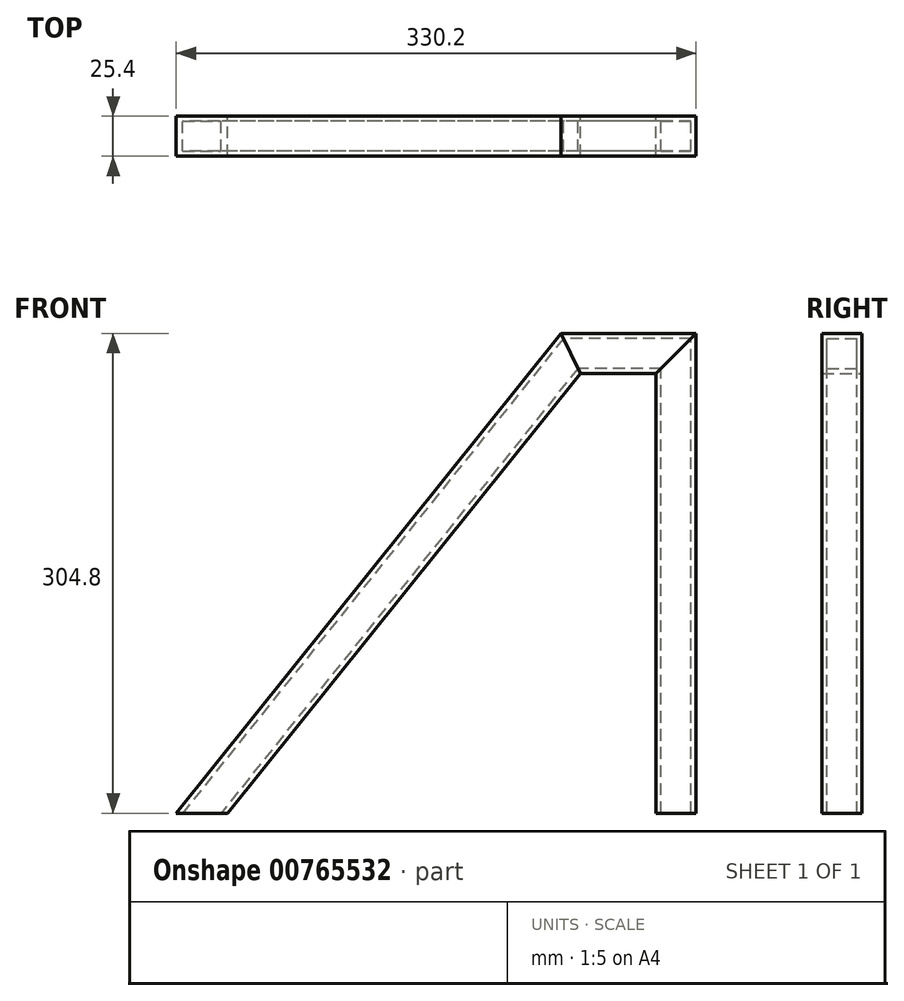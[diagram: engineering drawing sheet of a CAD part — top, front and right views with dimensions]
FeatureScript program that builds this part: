
annotation { "Feature Type Name" : "Feature", "Feature Type Description" : "" }
export const myFeature = defineFeature(function(context is Context, id is Id, definition is map)
    precondition{}
    {
        {
            var Q0;
            Q0=qCreatedBy(makeId("Front.planeOp"),FACE);
            var sketch = newSketch(context, id + "F0", { "sketchPlane" : qUnion([Q0])});
            skLineSegment(sketch, "E0", {"start": v(0, 0) * mm, "end": v(0, 304.8) * mm});
            skLineSegment(sketch, "E1", {"start": v(0, 304.8) * mm, "end": v(-85.72, 304.8) * mm});
            skLineSegment(sketch, "E2", {"start": v(-85.72, 304.8) * mm, "end": v(-330.2, 0) * mm});
            skLineSegment(sketch, "E3.0", {"start": v(-73.54, 279.4) * mm, "end": v(-297.64, 0) * mm});
            skLineSegment(sketch, "E3.1", {"start": v(-25.4, 279.4) * mm, "end": v(-73.54, 279.4) * mm});
            skLineSegment(sketch, "E3.2", {"start": v(-25.4, 0) * mm, "end": v(-25.4, 279.4) * mm});
            skLineSegment(sketch, "E4", {"start": v(-330.2, 0) * mm, "end": v(-297.64, 0) * mm});
            skLineSegment(sketch, "E5", {"start": v(-25.4, 0) * mm, "end": v(0, 0) * mm});
            skLineSegment(sketch, "E6", {"start": v(-25.4, 279.4) * mm, "end": v(0, 304.8) * mm});
            skLineSegment(sketch, "E7", {"start": v(-73.54, 279.4) * mm, "end": v(-85.73, 304.8) * mm});
            skSolve(sketch);
        }
        {
            var Q0;
            Q0=makeQuery(id+"F0.imprint","IMPRINT",FACE,{"disambiguationData":[TD([[makeQuery(id+"F0.imprint","IMPRINT",EDGE,{"derivedFrom":sQuery(id+"F0.wireOp",EDGE,"E2")}),1.0]])]});
            extrude(context, id + "F1", {"entities" : qUnion([Q0]), "depth" : 25.4 * mm, "offsetDistance" : 25.4 * mm, "symmetric" : true});
        }
        {
            var Q0;
            Q0=makeQuery(id+"F0.imprint","IMPRINT",FACE,{"disambiguationData":[TD([[makeQuery(id+"F0.imprint","IMPRINT",EDGE,{"derivedFrom":sQuery(id+"F0.wireOp",EDGE,"E1")}),1.0]])]});
            extrude(context, id + "F2", {"entities" : qUnion([Q0]), "depth" : 25.4 * mm, "offsetDistance" : 25.4 * mm, "symmetric" : true});
        }
        {
            var Q0;
            Q0=makeQuery(id+"F0.imprint","IMPRINT",FACE,{"disambiguationData":[TD([[makeQuery(id+"F0.imprint","IMPRINT",EDGE,{"derivedFrom":sQuery(id+"F0.wireOp",EDGE,"E0")}),1.0]])]});
            extrude(context, id + "F3", {"entities" : qUnion([Q0]), "depth" : 25.4 * mm, "offsetDistance" : 25.4 * mm, "symmetric" : true});
        }
        {
            var Q0;
            Q0=makeQuery(id+"F1.opExtrude","SWEPT_FACE",FACE,{"disambiguationData":[OSD([sQuery(id+"F0.wireOp",EDGE,"E7")])]});
            var Q1;
            Q1=makeQuery(id+"F1.opExtrude","SWEPT_FACE",FACE,{"disambiguationData":[OSD([sQuery(id+"F0.wireOp",EDGE,"E4")])]});
            shell(context, id + "F4", {"entities" : qUnion([Q0, Q1]), "thickness" : 3.17 * mm});
        }
        {
            var Q0;
            Q0=makeQuery(id+"F2.opExtrude","SWEPT_FACE",FACE,{"disambiguationData":[OSD([sQuery(id+"F0.wireOp",EDGE,"E7")])]});
            var Q1;
            Q1=makeQuery(id+"F2.opExtrude","SWEPT_FACE",FACE,{"disambiguationData":[OSD([sQuery(id+"F0.wireOp",EDGE,"E6")])]});
            shell(context, id + "F5", {"entities" : qUnion([Q0, Q1]), "thickness" : 3.17 * mm});
        }
        {
            var Q0;
            Q0=makeQuery(id+"F3.opExtrude","SWEPT_FACE",FACE,{"disambiguationData":[OSD([sQuery(id+"F0.wireOp",EDGE,"E6")])]});
            var Q1;
            Q1=makeQuery(id+"F3.opExtrude","SWEPT_FACE",FACE,{"disambiguationData":[OSD([sQuery(id+"F0.wireOp",EDGE,"E5")])]});
            var Q2;
            Q2=makeQuery(id+"F3.opExtrude","SWEPT_BODY",BODY,{"disambiguationData":[OSD([sQuery(id+"F0.wireOp",EDGE,"E0"),sQuery(id+"F0.wireOp",EDGE,"E3.2"),sQuery(id+"F0.wireOp",EDGE,"E5"),sQuery(id+"F0.wireOp",EDGE,"E6")])]});
            shell(context, id + "F6", {"entities" : qUnion([Q0, Q1]), "parts" : qUnion([Q2]), "thickness" : 3.17 * mm});
        }
    });
